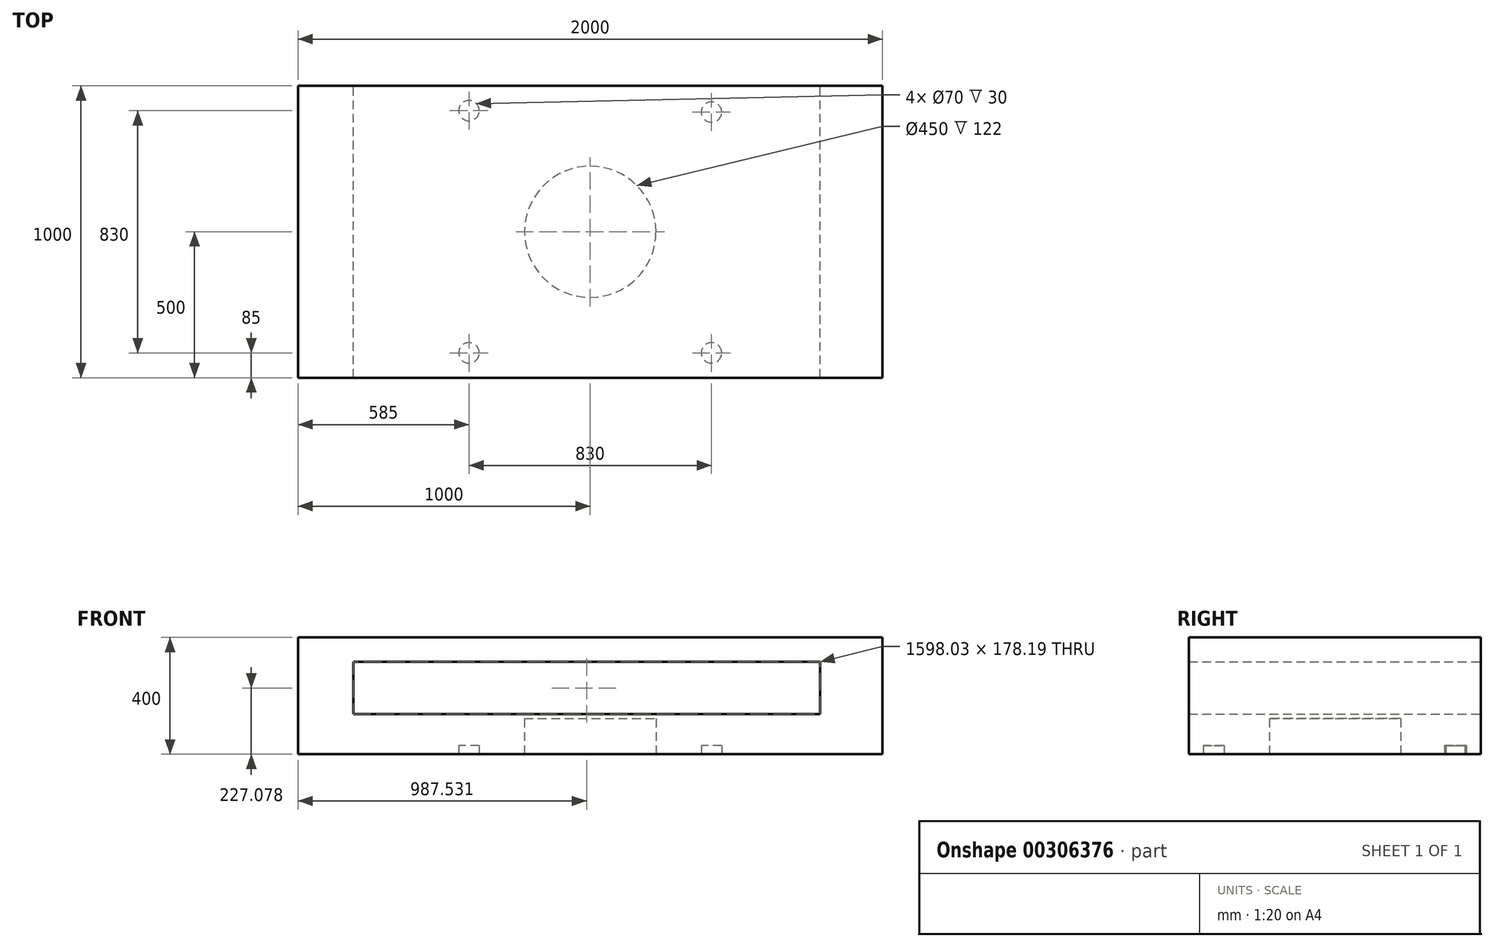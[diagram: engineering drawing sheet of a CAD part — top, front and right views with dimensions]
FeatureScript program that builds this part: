
annotation { "Feature Type Name" : "Feature", "Feature Type Description" : "" }
export const myFeature = defineFeature(function(context is Context, id is Id, definition is map)
    precondition{}
    {
        {
            var Q0;
            Q0=qCreatedBy(makeId("Front.planeOp"),FACE);
            var sketch = newSketch(context, id + "F0", { "sketchPlane" : qUnion([Q0])});
            skLineSegment(sketch, "E0.bottom", {"start": v(0, 0) * mm, "end": v(-2000, 0) * mm});
            skLineSegment(sketch, "E0.top", {"start": v(0, 425) * mm, "end": v(-2000, 425) * mm});
            skLineSegment(sketch, "E0.left", {"start": v(0, 0) * mm, "end": v(0, 425) * mm});
            skLineSegment(sketch, "E0.right", {"start": v(-2000, 0) * mm, "end": v(-2000, 425) * mm});
            skLineSegment(sketch, "E1.bottom", {"start": v(-1811.49, 316.17) * mm, "end": v(-213.45, 316.17) * mm});
            skLineSegment(sketch, "E1.top", {"start": v(-1811.49, 137.98) * mm, "end": v(-213.45, 137.98) * mm});
            skLineSegment(sketch, "E1.left", {"start": v(-1811.49, 316.17) * mm, "end": v(-1811.49, 137.98) * mm});
            skLineSegment(sketch, "E1.right", {"start": v(-213.45, 316.17) * mm, "end": v(-213.45, 137.98) * mm});
            skSolve(sketch);
        }
        {
            var Q0;
            Q0=makeQuery(id+"F0.imprint","IMPRINT",FACE,{"disambiguationData":[TD([[makeQuery(id+"F0.imprint","IMPRINT",EDGE,{"derivedFrom":sQuery(id+"F0.wireOp",EDGE,"E0.bottom")}),-1.0]])]});
            extrude(context, id + "F1", {"entities" : qUnion([Q0]), "depth" : 1000 * mm});
        }
        {
            var Q0;
            Q0=makeQuery(id+"F1.opExtrude","SWEPT_FACE",FACE,{"disambiguationData":[OSD([sQuery(id+"F0.wireOp",EDGE,"E0.top")])]});
            extrude(context, id + "F2", {"entities" : qUnion([Q0]), "operationType" : NewBodyOperationType.REMOVE, "oppositeDirection" : true, "depth" : 25 * mm});
        }
        {
            var Q0;
            Q0=qCreatedBy(makeId("Top.planeOp"),FACE);
            var sketch = newSketch(context, id + "F3", { "sketchPlane" : qUnion([Q0])});
            skCircle(sketch, "E2", {"center": v(-1415, -85) * mm, "radius": 35 * mm});
            skCircle(sketch, "E3", {"center": v(-585, -90) * mm, "radius": 35 * mm});
            skCircle(sketch, "E4", {"center": v(-1415, -915) * mm, "radius": 35 * mm});
            skCircle(sketch, "E5", {"center": v(-585, -915) * mm, "radius": 35 * mm});
            skSolve(sketch);
        }
        {
            var Q0;
            Q0=makeQuery(id+"F3.imprint","IMPRINT",FACE,{"disambiguationData":[TD([[makeQuery(id+"F3.imprint","IMPRINT",EDGE,{"derivedFrom":sQuery(id+"F3.wireOp",EDGE,"E2")}),1.0]])]});
            var Q1;
            Q1=makeQuery(id+"F3.imprint","IMPRINT",FACE,{"disambiguationData":[TD([[makeQuery(id+"F3.imprint","IMPRINT",EDGE,{"derivedFrom":sQuery(id+"F3.wireOp",EDGE,"E4")}),1.0]])]});
            var Q2;
            Q2=makeQuery(id+"F3.imprint","IMPRINT",FACE,{"disambiguationData":[TD([[makeQuery(id+"F3.imprint","IMPRINT",EDGE,{"derivedFrom":sQuery(id+"F3.wireOp",EDGE,"E5")}),1.0]])]});
            var Q3;
            Q3=makeQuery(id+"F3.imprint","IMPRINT",FACE,{"disambiguationData":[TD([[makeQuery(id+"F3.imprint","IMPRINT",EDGE,{"derivedFrom":sQuery(id+"F3.wireOp",EDGE,"E3")}),1.0]])]});
            extrude(context, id + "F4", {"entities" : qUnion([Q0, Q1, Q2, Q3]), "operationType" : NewBodyOperationType.REMOVE, "depth" : 30 * mm});
        }
        {
            var Q0;
            Q0=makeQuery(id+"F1.opExtrude","SWEPT_FACE",FACE,{"disambiguationData":[OSD([sQuery(id+"F0.wireOp",EDGE,"E0.bottom")])]});
            var sketch = newSketch(context, id + "F5", { "sketchPlane" : qUnion([Q0])});
            skCircle(sketch, "E6", {"center": v(-1000, 500) * mm, "radius": 225 * mm});
            skSolve(sketch);
        }
        {
            var Q0;
            Q0=makeQuery(id+"F5.imprint","IMPRINT",FACE,{"disambiguationData":[TD([[makeQuery(id+"F5.imprint","IMPRINT",EDGE,{"derivedFrom":sQuery(id+"F5.wireOp",EDGE,"E6")}),1.0]])]});
            extrude(context, id + "F6", {"entities" : qUnion([Q0]), "operationType" : NewBodyOperationType.REMOVE, "oppositeDirection" : true, "depth" : 122 * mm});
        }
    });
